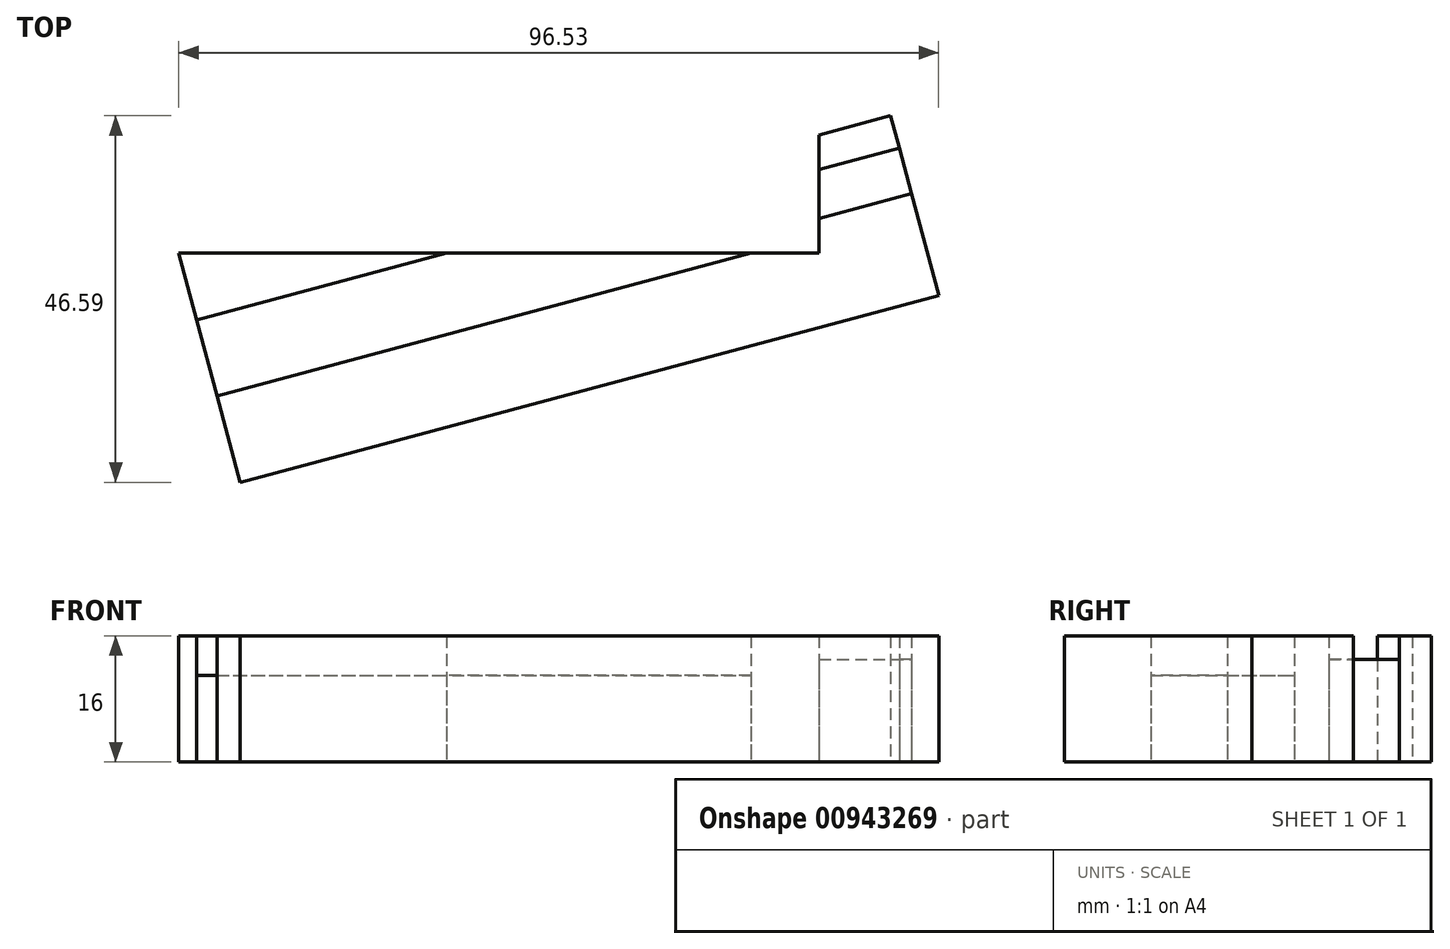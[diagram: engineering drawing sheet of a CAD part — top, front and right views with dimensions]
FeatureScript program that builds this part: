
annotation { "Feature Type Name" : "Feature", "Feature Type Description" : "" }
export const myFeature = defineFeature(function(context is Context, id is Id, definition is map)
    precondition{}
    {
        {
            assignVariable(context, id + "F0", {"name" : "drill_guide_small_d", "anyValue" : 6});
        }
        {
            assignVariable(context, id + "F1", {"name" : "drill_guide_big_d", "anyValue" : 10});
        }
        {
            var Q0;
            Q0=qCreatedBy(makeId("Top.planeOp"),FACE);
            var sketch = newSketch(context, id + "F2", { "sketchPlane" : qUnion([Q0])});
            skLineSegment(sketch, "E0", {"start": v(0, 0) * mm, "end": v(0, -7.5) * mm});
            skLineSegment(sketch, "E1", {"start": v(0, -7.5) * mm, "end": v(-81.33, -7.5) * mm});
            skLineSegment(sketch, "E2", {"start": v(-81.33, -7.5) * mm, "end": v(-73.52, -36.65) * mm});
            skLineSegment(sketch, "E3", {"start": v(-73.52, -36.65) * mm, "end": v(15.2, -12.88) * mm});
            skLineSegment(sketch, "E4", {"start": v(15.2, -12.88) * mm, "end": v(9.1, 9.94) * mm});
            skLineSegment(sketch, "E5", {"start": v(9.1, 9.94) * mm, "end": v(0, 7.5) * mm});
            skLineSegment(sketch, "E6", {"start": v(0, 7.5) * mm, "end": v(0, 0) * mm});
            skLineSegment(sketch, "E7", {"start": v(0, -3.1) * mm, "end": v(11.74, 0.04) * mm});
            skLineSegment(sketch, "E8", {"start": v(0, 3.1) * mm, "end": v(10.19, 5.84) * mm});
            skLineSegment(sketch, "E9", {"start": v(-76.46, -25.67) * mm, "end": v(-8.67, -7.5) * mm});
            skLineSegment(sketch, "E10", {"start": v(-79.05, -16) * mm, "end": v(-47.3, -7.5) * mm});
            skSolve(sketch);
        }
        {
            assignVariable(context, id + "F3", {"name" : "h", "anyValue" : 16});
        }
        {
            var Q0;
            {var subQ0=sQuery(id+"F2.wireOp",EDGE,"E3");Q0=makeQuery(id+"F2.imprint","IMPRINT",FACE,{"disambiguationData":[TD([[makeQuery(id+"F2.imprint","IMPRINT",EDGE,{"derivedFrom":subQ0}),1.0]])]});}
            var Q1;
            {var subQ3=sQuery(id+"F2.wireOp",EDGE,"E10");Q1=makeQuery(id+"F2.imprint","IMPRINT",FACE,{"disambiguationData":[TD([[makeQuery(id+"F2.imprint","IMPRINT",EDGE,{"derivedFrom":subQ3}),1.0]])]});}
            var Q2;
            {var subQ0=sQuery(id+"F2.wireOp",EDGE,"E5");Q2=makeQuery(id+"F2.imprint","IMPRINT",FACE,{"disambiguationData":[TD([[makeQuery(id+"F2.imprint","IMPRINT",EDGE,{"derivedFrom":subQ0}),1.0]])]});}
            extrude(context, id + "F4", {"entities" : qUnion([Q0, Q1, Q2]), "depth" : (getVariable(context, 'h')) * mm, "offsetDistance" : 25 * mm});
        }
        {
            var Q0;
            {var subQ0=sQuery(id+"F2.wireOp",EDGE,"E9");Q0=makeQuery(id+"F2.imprint","IMPRINT",FACE,{"disambiguationData":[TD([[makeQuery(id+"F2.imprint","IMPRINT",EDGE,{"derivedFrom":subQ0}),1.0]])]});}
            extrude(context, id + "F5", {"entities" : qUnion([Q0]), "depth" : (getVariable(context, 'h') - getVariable(context, 'drill_guide_big_d') / 2) * mm, "offsetDistance" : 25 * mm});
        }
        {
            var Q0;
            {var subQ4=sQuery(id+"F2.wireOp",EDGE,"E7");Q0=makeQuery(id+"F2.imprint","IMPRINT",FACE,{"disambiguationData":[TD([[makeQuery(id+"F2.imprint","IMPRINT",EDGE,{"derivedFrom":subQ4}),1.0]])]});}
            extrude(context, id + "F6", {"entities" : qUnion([Q0]), "depth" : (getVariable(context, 'h') - getVariable(context, 'drill_guide_small_d') / 2) * mm, "offsetDistance" : 25 * mm});
        }
    });
